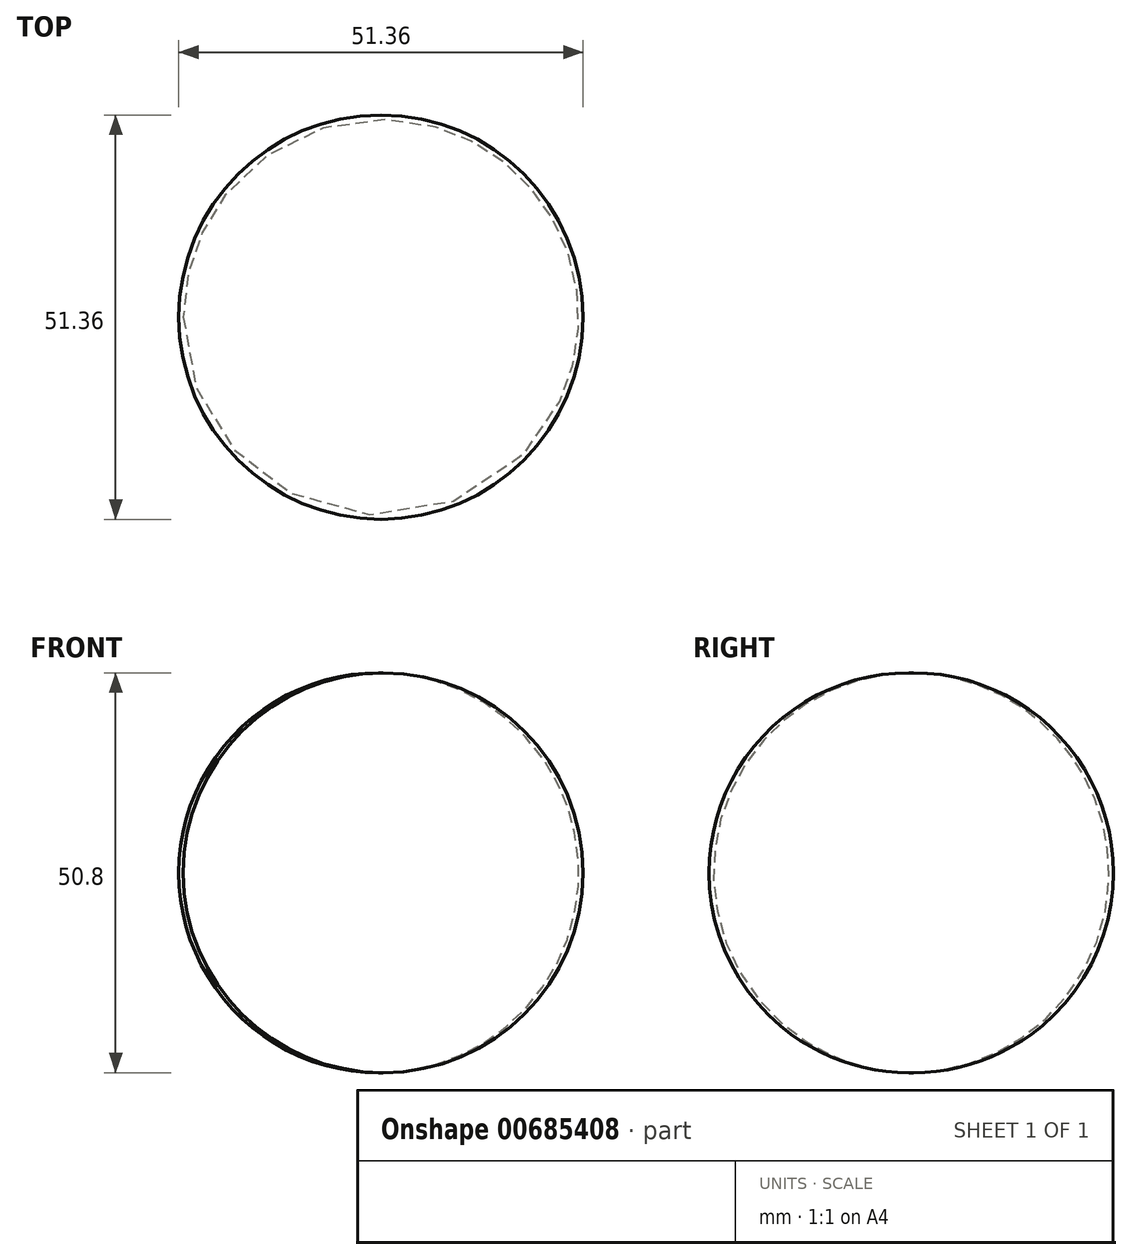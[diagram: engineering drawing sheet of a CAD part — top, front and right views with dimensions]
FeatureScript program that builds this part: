
annotation { "Feature Type Name" : "Feature", "Feature Type Description" : "" }
export const myFeature = defineFeature(function(context is Context, id is Id, definition is map)
    precondition{}
    {
        {
            var Q0;
            Q0=qCreatedBy(makeId("Front.planeOp"),FACE);
            var sketch = newSketch(context, id + "F0", { "sketchPlane" : qUnion([Q0])});
            skArc(sketch, "E0", {"start": v(0, 0) * mm, "mid": v(25.12, 25.4) * mm, "end": v(0, 50.8) * mm});
            skLineSegment(sketch, "E1", {"start": v(0, 50.8) * mm, "end": v(0, 0) * mm});
            skSolve(sketch);
        }
        {
            var Q0;
            Q0=makeQuery(id+"F0.imprint","IMPRINT",FACE,{"disambiguationData":[TD([[makeQuery(id+"F0.imprint","IMPRINT",EDGE,{"derivedFrom":sQuery(id+"F0.wireOp",EDGE,"E0")}),1.0]])]});
            var Q1;
            Q1=sQuery(id+"F0.wireOp",EDGE,"E1");
            revolve(context, id + "F1", {"entities" : qUnion([Q0]), "axis" : qUnion([Q1]), "revolveType" : RevolveType.FULL});
        }
    });
